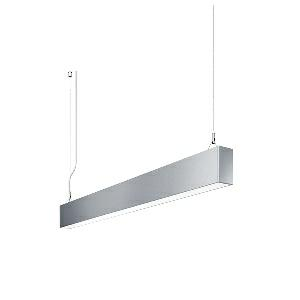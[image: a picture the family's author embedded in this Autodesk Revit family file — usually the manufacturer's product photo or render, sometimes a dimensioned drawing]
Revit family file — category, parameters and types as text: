
# Revit family: dotoo_line_-_dlp_1500_840_d_00805821_e019
name_source: partatom
category: Lighting Fixtures
units: mm (PartAtom-declared; Revit-internal decimal feet)

## family parameters
Cut with Voids When Loaded = No
Host = Face
Light Source = No
Part Type = Normal
Room Calculation Point = No
Round Connector Dimension = Use Diameter
Shared = No

## types (1)
- DOTOO.line - DLP 1500/840/D (1 x LED, 1350 lm, 4000K)
    Apparent Load = 13 VA
    Approval mark = CE
    CIE Flux Codes = 67 91 98 100 100
    Color Rendering = 80-89
    Color Temperature = 4000K
    Control Gear = Electronic ballast
    Default Elevation = 1800 mm
    Description = DLP 1500/840/D|Suspended luminaire|light source: LED|connected load: 220-240 V, 50/60 Hz|Power consumption: approx. 13 W|standby: approx. 0,20|luminous flux: 1350 lm|luminous efficacy: 103 lm/W|light distribution: Direct|direct ratio: approx. 100 %|colour temperature: Cold white, ca. 4000 K|color rendering index (CRI): >= 80|chromaticity tolerance:  3 SDCM|System of protection: IP 40|technology: Continuously dimmable|luminaire body|material: Sectional aluminium|colour: Silver|lamp cover: Acrylic (PMMA), Clear|mains lead: 2.00 m With free stranded wires|Fastening: Steel cable 0.3 - 0.7 m|glare control: Prism aperture|luminance(L65): <= 3000 cd/m|unified glare rating(4H 8H): <=  19|special features: DALI Load 1x, TouchDIM - dimming via standard switch, Flicker-free, Suitable as emergency lighting|
    Frequency = 50 Hz
    Height = 110 mm
    Lamp = 1 x LED
    Lamp Light Flux = 1350 lm
    Lamp count = 1
    Length = 1134 mm
    Luminous efficacy = 104 lm/W
    Manufacturer = Waldmann
    ModVariant = No
    Model = 00805821
    Mounting Place = Ceiling
    Mounting Type = Pendant
    Number of Poles = 1
    OnlyDefault = Yes
    Power Factor = 1
    Product Name = DOTOO.line - DLP 1500/840/D
    Product group = Suspended luminaire
    ProductGroupID = 9
    Protection Class = Protection class I
    Protection Degree = IP 40
    RLX_Detail_Level = 1
    RLX_Emergency_Light_Flux = 0 lm
    RLX_Emergency_Type = 0
    RLX_Emergency_Type_DB = No
    RlxData = <blob elided: 21057 chars, md5=f1faafcc>
    Socket = socket
    Standby Power = 0 W
    System Light Flux = 1350 lm
    System Power = 13 W
    Type Comments = Product without accessories
    Type Image = 113290000-00692519.jpg
    URL = http://relux.com
    VarID = ---
    Voltage = 230 V
    Voltage Range = 220-240 V
    Weight = 0.00 kg
    Width = 60 mm  [stored 0.19685 ft]

note: [stored X ft] marks values corroborated as IEEE doubles in the binary element streams (Revit-internal decimal feet)

## geometry (parser evidence)
native form markers: Blend x4, Sweep x12
no freeform markers — native parametric forms only
